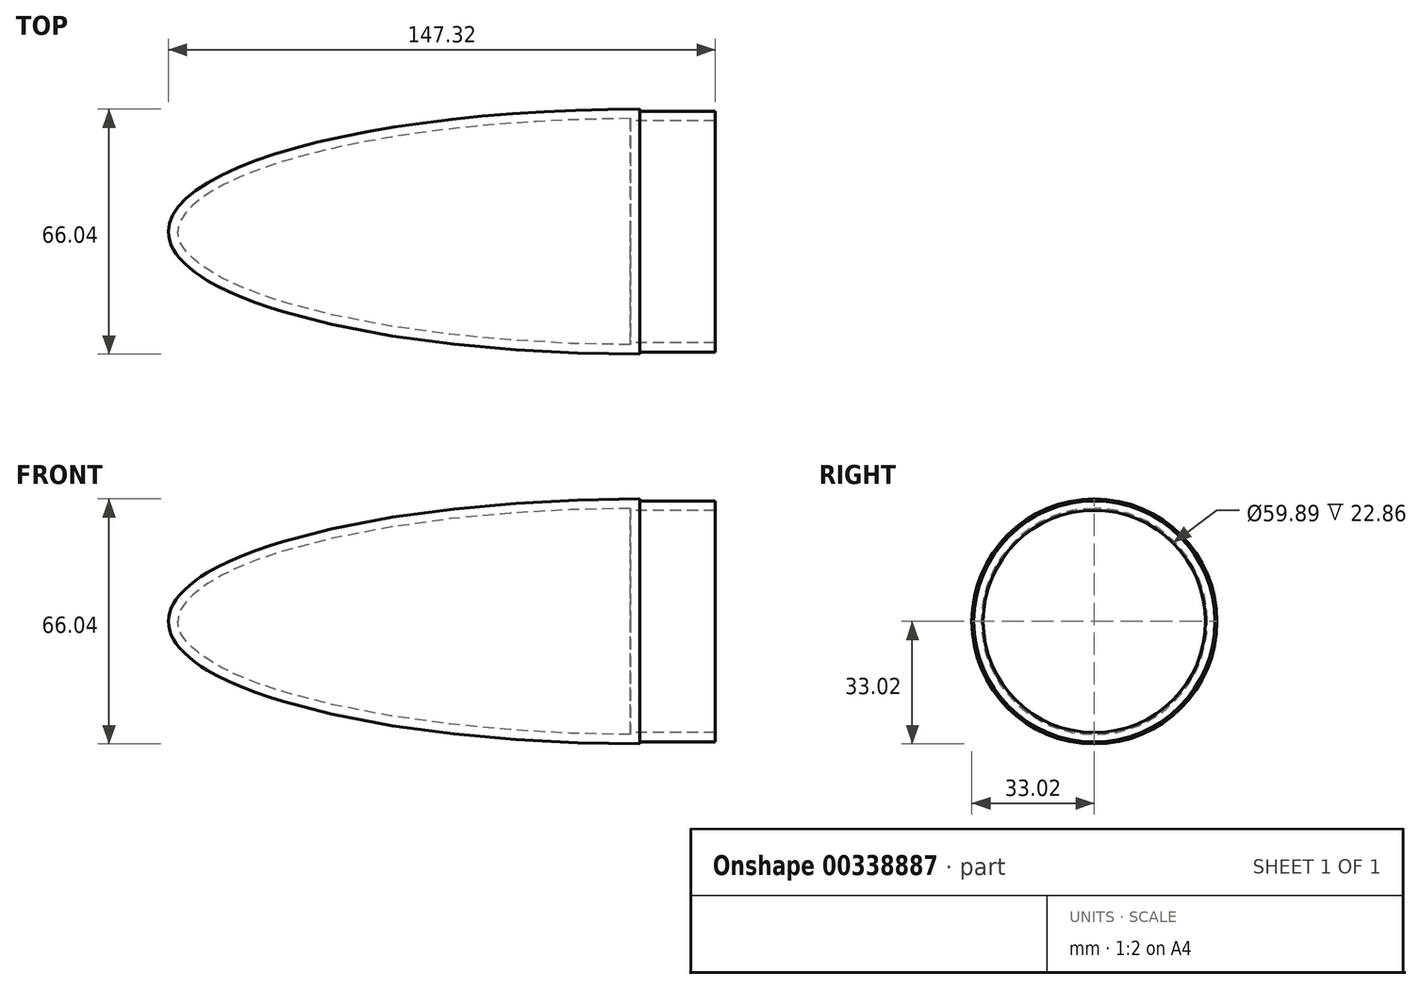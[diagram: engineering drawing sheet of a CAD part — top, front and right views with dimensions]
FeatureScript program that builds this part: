
annotation { "Feature Type Name" : "Feature", "Feature Type Description" : "" }
export const myFeature = defineFeature(function(context is Context, id is Id, definition is map)
    precondition{}
    {
        {
            var Q0;
            Q0=qCreatedBy(makeId("Top.planeOp"),FACE);
            var sketch = newSketch(context, id + "F0", { "sketchPlane" : qUnion([Q0])});
            skEllipticalArc(sketch, "E0", {});
            skLineSegment(sketch, "E1", {"start": v(0, 33.02) * mm, "end": v(0, 0) * mm});
            skLineSegment(sketch, "E2.bottom", {"start": v(0, 32.49) * mm, "end": v(20.32, 32.49) * mm});
            skLineSegment(sketch, "E2.left", {"start": v(0, 32.49) * mm, "end": v(0, 0) * mm});
            skLineSegment(sketch, "E2.right", {"start": v(20.32, 32.49) * mm, "end": v(20.32, 0) * mm});
            skLineSegment(sketch, "E3", {"start": v(-127, 0) * mm, "end": v(20.32, 0) * mm});
            skPoint(sketch, "E2.top.end.orphan", {"position": v(20.32, -32.49) * mm});
            skPoint(sketch, "E4.orphan", {"position": v(0, -32.49) * mm});
            skLineSegment(sketch, "E5.trimOffspring", {"start": v(0, -32.49) * mm, "end": v(0, -33.02) * mm});
            const initialGuessF0  = {"E0": [0, 0, -1, 0, 0.127, 0.03302, 4.71238898038469, 0]};
            skSetInitialGuess(sketch, initialGuessF0);
            skSolve(sketch);
        }
        {
            var Q0;
            {var subQ0=sQuery(id+"F0.wireOp",EDGE,"E3");var subQ1=sQuery(id+"F0.wireOp",EDGE,"E0");var subQ2=makeQuery(id+"F0.imprint","INTERSECT",VERTEX,{"derivedFrom":[subQ1,subQ0]});Q0=makeQuery(id+"F0.imprint","IMPRINT",FACE,{"disambiguationData":[TD([[makeQuery(id+"F0.imprint","IMPRINT",EDGE,{"disambiguationData":[TD([[subQ2,1.0]])],"derivedFrom":subQ1}),1.0]])]});}
            var Q1;
            {var subQ0=sQuery(id+"F0.wireOp",EDGE,"E2.bottom");Q1=makeQuery(id+"F0.imprint","IMPRINT",FACE,{"disambiguationData":[TD([[makeQuery(id+"F0.imprint","IMPRINT",EDGE,{"derivedFrom":subQ0}),-1.0]])]});}
            var Q2;
            Q2=sQuery(id+"F0.wireOp",EDGE,"E3");
            revolve(context, id + "F1", {"entities" : qUnion([Q0, Q1]), "axis" : qUnion([Q2]), "revolveType" : RevolveType.FULL});
        }
        {
            var Q0;
            Q0=makeQuery(id+"F1.opRevolve","SWEPT_FACE",FACE,{"disambiguationData":[OSD([sQuery(id+"F0.wireOp",EDGE,"E2.right")])]});
            shell(context, id + "F2", {"entities" : qUnion([Q0]), "thickness" : 2.54 * mm});
        }
    });
